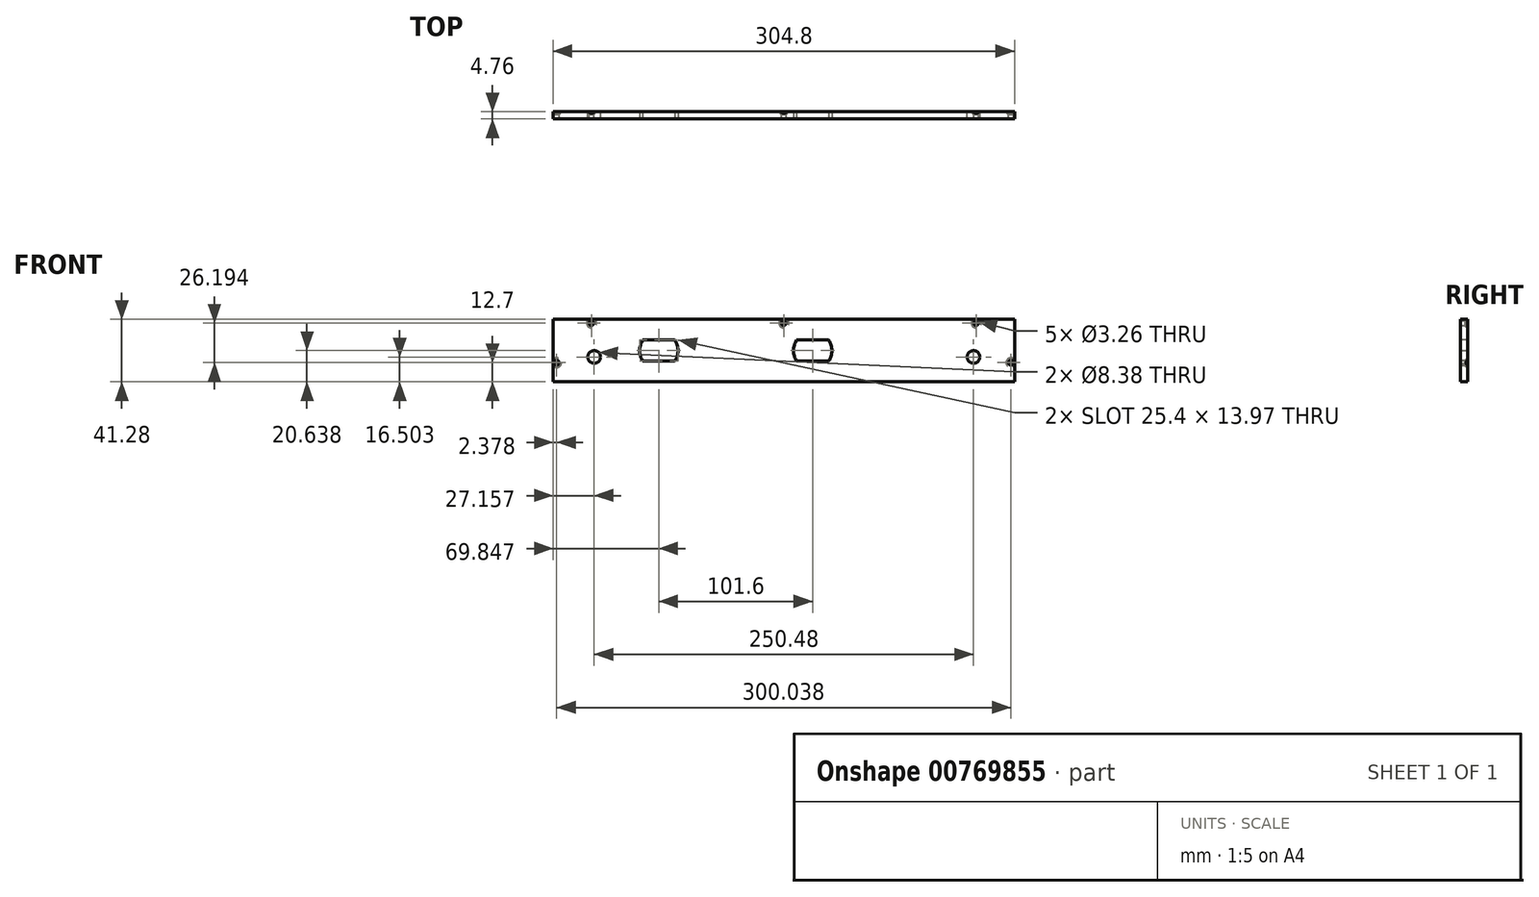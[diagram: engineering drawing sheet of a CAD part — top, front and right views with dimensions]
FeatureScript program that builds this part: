
annotation { "Feature Type Name" : "Feature", "Feature Type Description" : "" }
export const myFeature = defineFeature(function(context is Context, id is Id, definition is map)
    precondition{}
    {
        {
            var Q0;
            Q0=qCreatedBy(makeId("Front.planeOp"),FACE);
            var sketch = newSketch(context, id + "F0", { "sketchPlane" : qUnion([Q0])});
            skLineSegment(sketch, "E0.bottom", {"start": v(-119.12, 56.77) * mm, "end": v(185.68, 56.77) * mm});
            skLineSegment(sketch, "E0.top", {"start": v(-119.12, 15.5) * mm, "end": v(185.68, 15.5) * mm});
            skLineSegment(sketch, "E0.left", {"start": v(-119.12, 56.77) * mm, "end": v(-119.12, 15.5) * mm});
            skLineSegment(sketch, "E0.right", {"start": v(185.68, 56.77) * mm, "end": v(185.68, 15.5) * mm});
            skSolve(sketch);
        }
        {
            var Q0;
            Q0=qSketchRegion(id+"F0",true);
            extrude(context, id + "F1", {"entities" : qUnion([Q0]), "depth" : 4.76 * mm, "offsetDistance" : 25.4 * mm});
        }
        {
            var Q0;
            Q0=makeQuery(id+"F1.opExtrude","CAP_FACE",FACE,{"disambiguationData":[OSD([sQuery(id+"F0.wireOp",EDGE,"E0.bottom"),sQuery(id+"F0.wireOp",EDGE,"E0.top"),sQuery(id+"F0.wireOp",EDGE,"E0.left"),sQuery(id+"F0.wireOp",EDGE,"E0.right")])],"isStart":true});
            var sketch = newSketch(context, id + "F2", { "sketchPlane" : qUnion([Q0])});
            skLineSegment(sketch, "E1", {"start": v(116.74, 56.77) * mm, "end": v(116.74, 15.5) * mm, "construction": true});
            skLineSegment(sketch, "E2", {"start": v(119.12, 54.38) * mm, "end": v(-185.68, 54.38) * mm, "construction": true});
            skLineSegment(sketch, "E3", {"start": v(-183.3, 15.5) * mm, "end": v(-183.3, 56.77) * mm, "construction": true});
            skPoint(sketch, "E4", {"position": v(116.74, 28.2) * mm});
            skPoint(sketch, "E5", {"position": v(-183.3, 28.2) * mm});
            skPoint(sketch, "E6", {"position": v(-160.28, 54.38) * mm});
            skPoint(sketch, "E7", {"position": v(-33.28, 54.38) * mm});
            skPoint(sketch, "E8", {"position": v(93.72, 54.38) * mm});
            skSolve(sketch);
        }
        {
            var Q0;
            Q0=makeQuery(id+"F1.opExtrude","CAP_FACE",FACE,{"disambiguationData":[OSD([sQuery(id+"F0.wireOp",EDGE,"E0.bottom"),sQuery(id+"F0.wireOp",EDGE,"E0.top"),sQuery(id+"F0.wireOp",EDGE,"E0.left"),sQuery(id+"F0.wireOp",EDGE,"E0.right")])],"isStart":true});
            var sketch = newSketch(context, id + "F3", { "sketchPlane" : qUnion([Q0])});
            skLineSegment(sketch, "E9", {"start": v(-185.68, 32) * mm, "end": v(119.12, 32) * mm, "construction": true});
            skPoint(sketch, "E10", {"position": v(-158.52, 32) * mm});
            skPoint(sketch, "E11", {"position": v(91.96, 32) * mm});
            skCircle(sketch, "E12", {"center": v(91.96, 32) * mm, "radius": 4.2 * mm});
            skCircle(sketch, "E13", {"center": v(-158.52, 32) * mm, "radius": 4.2 * mm});
            skSolve(sketch);
        }
        {
            var Q0;
            Q0 = qSketchRegion(id + "F3", true);
            extrude(context, id + "F4", {"entities" : qUnion([Q0]), "operationType" : NewBodyOperationType.REMOVE, "endBound" : BoundingType.THROUGH_ALL, "oppositeDirection" : true, "depth" : 25.4 * mm, "offsetDistance" : 25.4 * mm});
        }
        {
            var Q0;
            Q0=sQuery(id+"F2.wireOp",VERTEX,"E5");
            var Q1;
            Q1=sQuery(id+"F2.wireOp",VERTEX,"E6");
            var Q2;
            Q2=sQuery(id+"F2.wireOp",VERTEX,"E7");
            var Q3;
            Q3=sQuery(id+"F2.wireOp",VERTEX,"E8");
            var Q4;
            Q4=sQuery(id+"F2.wireOp",VERTEX,"E4");
            var Q5;
            Q5=makeQuery(id+"F1.opExtrude","SWEPT_BODY",BODY,{"disambiguationData":[OSD([sQuery(id+"F0.wireOp",EDGE,"E0.bottom"),sQuery(id+"F0.wireOp",EDGE,"E0.top"),sQuery(id+"F0.wireOp",EDGE,"E0.left"),sQuery(id+"F0.wireOp",EDGE,"E0.right")])]});
            hole(context, id + "F5", {"style" : HoleStyle.C_SINK, "endStyle" : HoleEndStyle.BLIND, "standardTappedOrClearance" : lookupTablePath({ "standard" : "ANSI", "fit" : "Normal (ASME)", "size" : "#4", "type" : "Clearance" }), "standardBlindInLast" : lookupTablePath({ "fit" : "Free", "standard" : "ANSI", "size" : "#4", "type" : "Clearance" }), "holeDiameter" : 3.26 * mm, "cSinkDiameter" : 6.48 * mm, "cSinkAngle" : 82 * degree, "majorDiameter" : 2.84 * mm, "holeDepth" : 14.6 * mm, "tappedDepth" : 12.7 * mm, "tapClearance" : 3, "locations" : qUnion([Q0, Q1, Q2, Q3, Q4]), "scope" : qUnion([Q5])});
        }
        {
            var Q0;
            Q0=makeQuery(id+"F1.opExtrude","CAP_FACE",FACE,{"disambiguationData":[OSD([sQuery(id+"F0.wireOp",EDGE,"E0.bottom"),sQuery(id+"F0.wireOp",EDGE,"E0.top"),sQuery(id+"F0.wireOp",EDGE,"E0.left"),sQuery(id+"F0.wireOp",EDGE,"E0.right")])],"isStart":false});
            var sketch = newSketch(context, id + "F6", { "sketchPlane" : qUnion([Q0])});
            skLineSegment(sketch, "E14", {"start": v(-119.12, 36.13) * mm, "end": v(185.68, 36.13) * mm, "construction": true});
            skArc(sketch, "E15", {"start": v(-59.88, 43.11) * mm, "mid": v(-61.97, 36.13) * mm, "end": v(-59.88, 29.14) * mm});
            skLineSegment(sketch, "E16", {"start": v(33.28, 56.77) * mm, "end": v(33.28, 15.5) * mm, "construction": true});
            skLineSegment(sketch, "E17.bottom", {"start": v(-59.88, 43.11) * mm, "end": v(-38.67, 43.11) * mm});
            skLineSegment(sketch, "E17.top", {"start": v(-59.88, 29.14) * mm, "end": v(-38.67, 29.14) * mm});
            skLineSegment(sketch, "E17.left", {"start": v(-59.88, 43.11) * mm, "end": v(-59.88, 29.14) * mm, "construction": true});
            skLineSegment(sketch, "E17.right", {"start": v(-38.67, 43.11) * mm, "end": v(-38.67, 29.14) * mm, "construction": true});
            skArc(sketch, "E18.trimOffspring", {"start": v(-38.67, 29.14) * mm, "mid": v(-36.57, 36.13) * mm, "end": v(-38.67, 43.11) * mm});
            skArc(sketch, "E19.MirrorCS", {"start": v(62.93, 43.11) * mm, "mid": v(65.03, 36.13) * mm, "end": v(62.93, 29.14) * mm});
            skLineSegment(sketch, "E20.MirrorCS", {"start": v(62.93, 43.11) * mm, "end": v(41.72, 43.11) * mm});
            skArc(sketch, "E21.MirrorCS", {"start": v(41.72, 29.14) * mm, "mid": v(39.63, 36.13) * mm, "end": v(41.72, 43.11) * mm});
            skLineSegment(sketch, "E22.MirrorCS", {"start": v(62.93, 29.14) * mm, "end": v(41.72, 29.14) * mm});
            skSolve(sketch);
        }
        {
            var Q0;
            Q0 = qSketchRegion(id + "F6", true);
            extrude(context, id + "F7", {"entities" : qUnion([Q0]), "operationType" : NewBodyOperationType.REMOVE, "oppositeDirection" : true, "depth" : 25.4 * mm, "offsetDistance" : 25.4 * mm});
        }
    });
